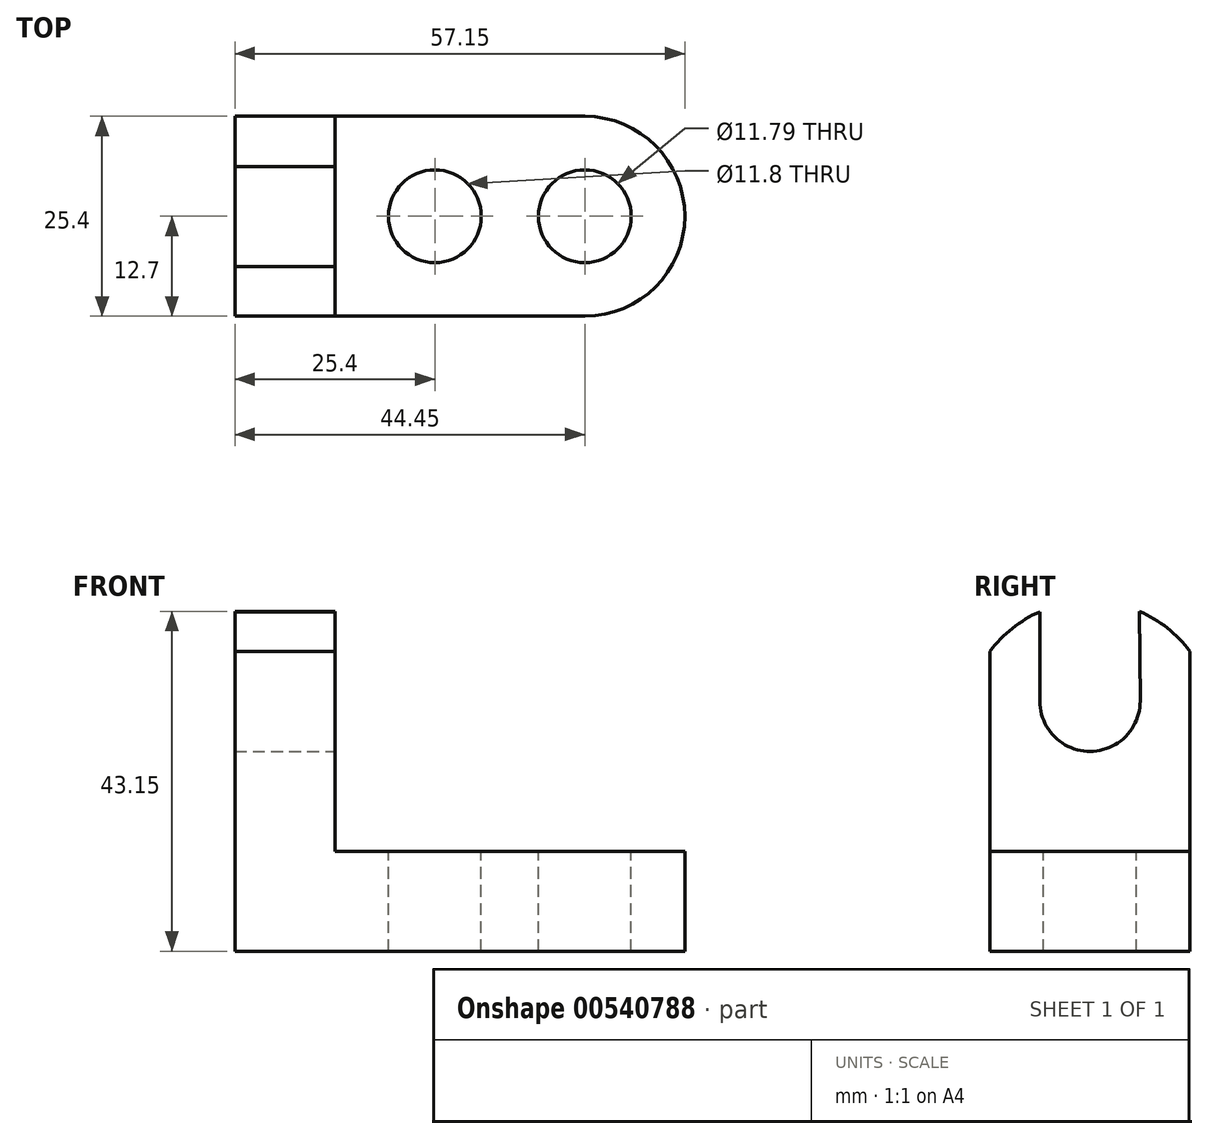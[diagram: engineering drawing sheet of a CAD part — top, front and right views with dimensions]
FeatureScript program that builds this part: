
annotation { "Feature Type Name" : "Feature", "Feature Type Description" : "" }
export const myFeature = defineFeature(function(context is Context, id is Id, definition is map)
    precondition{}
    {
        {
            var Q0;
            Q0=qCreatedBy(makeId("Front.planeOp"),FACE);
            var sketch = newSketch(context, id + "F0", { "sketchPlane" : qUnion([Q0])});
            skLineSegment(sketch, "E0", {"start": v(0, 0) * mm, "end": v(0, 44.45) * mm});
            skLineSegment(sketch, "E1", {"start": v(0, 44.45) * mm, "end": v(12.7, 44.45) * mm});
            skLineSegment(sketch, "E2", {"start": v(12.7, 44.45) * mm, "end": v(12.7, 12.7) * mm});
            skLineSegment(sketch, "E3", {"start": v(12.7, 12.7) * mm, "end": v(57.15, 12.7) * mm});
            skLineSegment(sketch, "E4", {"start": v(57.15, 12.7) * mm, "end": v(57.15, 0) * mm});
            skLineSegment(sketch, "E5", {"start": v(57.15, 0) * mm, "end": v(0, 0) * mm});
            skSolve(sketch);
        }
        {
            var Q0;
            Q0=makeQuery(id+"F0.imprint","IMPRINT",FACE,{"disambiguationData":[TD([[makeQuery(id+"F0.imprint","IMPRINT",EDGE,{"derivedFrom":sQuery(id+"F0.wireOp",EDGE,"E0")}),-1.0]])]});
            extrude(context, id + "F1", {"entities" : qUnion([Q0]), "depth" : 25.4 * mm, "offsetDistance" : 25.4 * mm});
        }
        {
            var Q0;
            Q0=makeQuery(id+"F1.opExtrude","SWEPT_FACE",FACE,{"disambiguationData":[OSD([sQuery(id+"F0.wireOp",EDGE,"E3")])]});
            var sketch = newSketch(context, id + "F2", { "sketchPlane" : qUnion([Q0])});
            skLineSegment(sketch, "E6", {"start": v(57.15, -12.7) * mm, "end": v(44.45, -12.7) * mm});
            skArc(sketch, "E7", {"start": v(44.45, -25.4) * mm, "mid": v(57.15, -12.7) * mm, "end": v(44.45, 0) * mm});
            skSolve(sketch);
        }
        {
            var Q0;
            {var subQ0=sQuery(id+"F2.wireOp",EDGE,"E7");var subQ1=sQuery(id+"F0.wireOp",EDGE,"E3");var subQ4=makeQuery(id+"F1.opExtrude","CAP_EDGE",EDGE,{"disambiguationData":[OSD([subQ1])],"isStart":true});var subQ5=makeQuery(id+"F2.imprint","INTERSECT",VERTEX,{"derivedFrom":[subQ4,subQ0]});Q0=makeQuery(id+"F2.imprint","IMPRINT",FACE,{"disambiguationData":[TD([[makeQuery(id+"F2.imprint","IMPRINT",EDGE,{"disambiguationData":[TD([[subQ5,1.0]])],"derivedFrom":subQ0}),-1.0]])]});}
            var Q1;
            {var subQ0=sQuery(id+"F2.wireOp",EDGE,"E7");var subQ1=sQuery(id+"F0.wireOp",EDGE,"E3");var subQ4=makeQuery(id+"F1.opExtrude","CAP_EDGE",EDGE,{"disambiguationData":[OSD([subQ1])],"isStart":false});var subQ5=makeQuery(id+"F2.imprint","INTERSECT",VERTEX,{"derivedFrom":[subQ4,subQ0]});Q1=makeQuery(id+"F2.imprint","IMPRINT",FACE,{"disambiguationData":[TD([[makeQuery(id+"F2.imprint","IMPRINT",EDGE,{"disambiguationData":[TD([[subQ5,-1.0]])],"derivedFrom":subQ0}),-1.0]])]});}
            extrude(context, id + "F3", {"entities" : qUnion([Q0, Q1]), "operationType" : NewBodyOperationType.REMOVE, "oppositeDirection" : true, "depth" : 25.4 * mm, "offsetDistance" : 25.4 * mm});
        }
        {
            var Q0;
            Q0=makeQuery(id+"F1.opExtrude","SWEPT_FACE",FACE,{"disambiguationData":[OSD([sQuery(id+"F0.wireOp",EDGE,"E2")])]});
            var sketch = newSketch(context, id + "F4", { "sketchPlane" : qUnion([Q0])});
            skLineSegment(sketch, "E8", {"start": v(-12.7, 44.45) * mm, "end": v(-12.7, 38.1) * mm});
            skArc(sketch, "E9", {"start": v(0, 38.1) * mm, "mid": v(-12.7, 44.45) * mm, "end": v(-25.4, 38.1) * mm});
            skSolve(sketch);
        }
        {
            var Q0;
            {var subQ0=sQuery(id+"F4.wireOp",EDGE,"E9");var subQ1=sQuery(id+"F0.wireOp",EDGE,"E2");var subQ4=makeQuery(id+"F1.opExtrude","CAP_EDGE",EDGE,{"disambiguationData":[OSD([subQ1])],"isStart":false});var subQ5=makeQuery(id+"F4.imprint","INTERSECT",VERTEX,{"derivedFrom":[subQ4,subQ0]});Q0=makeQuery(id+"F4.imprint","IMPRINT",FACE,{"disambiguationData":[TD([[makeQuery(id+"F4.imprint","IMPRINT",EDGE,{"disambiguationData":[TD([[subQ5,1.0]])],"derivedFrom":subQ0}),-1.0]])]});}
            var Q1;
            {var subQ0=sQuery(id+"F4.wireOp",EDGE,"E9");var subQ1=sQuery(id+"F0.wireOp",EDGE,"E2");var subQ4=makeQuery(id+"F1.opExtrude","CAP_EDGE",EDGE,{"disambiguationData":[OSD([subQ1])],"isStart":true});var subQ5=makeQuery(id+"F4.imprint","INTERSECT",VERTEX,{"derivedFrom":[subQ4,subQ0]});Q1=makeQuery(id+"F4.imprint","IMPRINT",FACE,{"disambiguationData":[TD([[makeQuery(id+"F4.imprint","IMPRINT",EDGE,{"disambiguationData":[TD([[subQ5,-1.0]])],"derivedFrom":subQ0}),-1.0]])]});}
            extrude(context, id + "F5", {"entities" : qUnion([Q0, Q1]), "operationType" : NewBodyOperationType.REMOVE, "oppositeDirection" : true, "depth" : 25.4 * mm, "offsetDistance" : 25.4 * mm});
        }
        {
            var Q0;
            Q0=makeQuery(id+"F1.opExtrude","SWEPT_FACE",FACE,{"disambiguationData":[OSD([sQuery(id+"F0.wireOp",EDGE,"E2")])]});
            var sketch = newSketch(context, id + "F6", { "sketchPlane" : qUnion([Q0])});
            skLineSegment(sketch, "E10", {"start": v(-12.7, 44.45) * mm, "end": v(-12.7, 31.75) * mm});
            skCircle(sketch, "E11", {"center": v(-12.7, 31.75) * mm, "radius": 6.37 * mm});
            skLineSegment(sketch, "E12", {"start": v(-12.7, 31.75) * mm, "end": v(-25.4, 31.75) * mm});
            skLineSegment(sketch, "E13", {"start": v(-19.07, 31.75) * mm, "end": v(-19.07, 43.12) * mm});
            skLineSegment(sketch, "E14", {"start": v(-6.33, 31.8) * mm, "end": v(0, 31.8) * mm});
            skLineSegment(sketch, "E15", {"start": v(-6.33, 31.8) * mm, "end": v(-6.4, 43.15) * mm});
            skLineSegment(sketch, "E16", {"start": v(-13.2, 25.4) * mm, "end": v(-13.2, 12.7) * mm});
            skLineSegment(sketch, "E17", {"start": v(-12.7, 31.75) * mm, "end": v(-13.2, 25.4) * mm});
            skSolve(sketch);
        }
        {
            var Q0;
            {var subQ8=sQuery(id+"F6.wireOp",EDGE,"E13");Q0=makeQuery(id+"F6.imprint","IMPRINT",FACE,{"disambiguationData":[TD([[makeQuery(id+"F6.imprint","IMPRINT",EDGE,{"derivedFrom":subQ8}),-1.0]])]});}
            var Q1;
            {var subQ8=sQuery(id+"F6.wireOp",EDGE,"E15");Q1=makeQuery(id+"F6.imprint","IMPRINT",FACE,{"disambiguationData":[TD([[makeQuery(id+"F6.imprint","IMPRINT",EDGE,{"derivedFrom":subQ8}),1.0]])]});}
            var Q2;
            {var subQ0=sQuery(id+"F6.wireOp",EDGE,"E12");var subQ1=sQuery(id+"F6.wireOp",EDGE,"E10");var subQ2=makeQuery(id+"F6.imprint","INTERSECT",VERTEX,{"derivedFrom":[subQ1,subQ0]});Q2=makeQuery(id+"F6.imprint","IMPRINT",FACE,{"disambiguationData":[TD([[makeQuery(id+"F6.imprint","IMPRINT",EDGE,{"disambiguationData":[TD([[subQ2,1.0]])],"derivedFrom":subQ1}),1.0]])]});}
            var Q3;
            {var subQ0=sQuery(id+"F6.wireOp",EDGE,"E12");var subQ1=sQuery(id+"F6.wireOp",EDGE,"E10");var subQ2=makeQuery(id+"F6.imprint","INTERSECT",VERTEX,{"derivedFrom":[subQ1,subQ0]});Q3=makeQuery(id+"F6.imprint","IMPRINT",FACE,{"disambiguationData":[TD([[makeQuery(id+"F6.imprint","IMPRINT",EDGE,{"disambiguationData":[TD([[subQ2,1.0]])],"derivedFrom":subQ1}),-1.0]])]});}
            var Q4;
            {var subQ3=sQuery(id+"F6.wireOp",EDGE,"E17");Q4=makeQuery(id+"F6.imprint","IMPRINT",FACE,{"disambiguationData":[TD([[makeQuery(id+"F6.imprint","IMPRINT",EDGE,{"derivedFrom":subQ3}),-1.0]])]});}
            extrude(context, id + "F7", {"entities" : qUnion([Q0, Q1, Q2, Q3, Q4]), "operationType" : NewBodyOperationType.REMOVE, "oppositeDirection" : true, "depth" : 25.4 * mm, "offsetDistance" : 25.4 * mm});
        }
        {
            var Q0;
            Q0=makeQuery(id+"F1.opExtrude","SWEPT_FACE",FACE,{"disambiguationData":[OSD([sQuery(id+"F0.wireOp",EDGE,"E3")])]});
            var sketch = newSketch(context, id + "F8", { "sketchPlane" : qUnion([Q0])});
            skCircle(sketch, "E18", {"center": v(25.4, -12.7) * mm, "radius": 5.9 * mm});
            skCircle(sketch, "E19", {"center": v(44.45, -12.7) * mm, "radius": 5.9 * mm});
            skLineSegment(sketch, "E20", {"start": v(25.4, -12.7) * mm, "end": v(25.4, -25.4) * mm});
            skLineSegment(sketch, "E21", {"start": v(44.45, -12.7) * mm, "end": v(44.45, -25.4) * mm});
            skLineSegment(sketch, "E22", {"start": v(25.4, -12.7) * mm, "end": v(57.15, -12.7) * mm});
            skLineSegment(sketch, "E23", {"start": v(44.45, -12.7) * mm, "end": v(57.15, -12.7) * mm});
            skSolve(sketch);
        }
        {
            var Q0;
            {var subQ0=sQuery(id+"F8.wireOp",EDGE,"E20");var subQ1=sQuery(id+"F8.wireOp",EDGE,"E18");var subQ2=makeQuery(id+"F8.imprint","INTERSECT",VERTEX,{"derivedFrom":[subQ1,subQ0]});Q0=makeQuery(id+"F8.imprint","IMPRINT",FACE,{"disambiguationData":[TD([[makeQuery(id+"F8.imprint","IMPRINT",EDGE,{"disambiguationData":[TD([[subQ2,1.0]])],"derivedFrom":subQ1}),1.0]])]});}
            var Q1;
            {var subQ0=sQuery(id+"F8.wireOp",EDGE,"E20");var subQ1=sQuery(id+"F8.wireOp",EDGE,"E18");var subQ2=makeQuery(id+"F8.imprint","INTERSECT",VERTEX,{"derivedFrom":[subQ1,subQ0]});Q1=makeQuery(id+"F8.imprint","IMPRINT",FACE,{"disambiguationData":[TD([[makeQuery(id+"F8.imprint","IMPRINT",EDGE,{"disambiguationData":[TD([[subQ2,-1.0]])],"derivedFrom":subQ1}),1.0]])]});}
            var Q2;
            {var subQ0=sQuery(id+"F8.wireOp",EDGE,"E23");var subQ1=sQuery(id+"F8.wireOp",EDGE,"E19");var subQ2=makeQuery(id+"F8.imprint","INTERSECT",VERTEX,{"derivedFrom":[subQ1,subQ0]});Q2=makeQuery(id+"F8.imprint","IMPRINT",FACE,{"disambiguationData":[TD([[makeQuery(id+"F8.imprint","IMPRINT",EDGE,{"disambiguationData":[TD([[subQ2,1.0]])],"derivedFrom":subQ1}),1.0]])]});}
            var Q3;
            {var subQ0=sQuery(id+"F8.wireOp",EDGE,"E22");var subQ1=sQuery(id+"F8.wireOp",EDGE,"E19");var subQ2=makeQuery(id+"F8.imprint","INTERSECT",VERTEX,{"derivedFrom":[subQ1,subQ0]});Q3=makeQuery(id+"F8.imprint","IMPRINT",FACE,{"disambiguationData":[TD([[makeQuery(id+"F8.imprint","IMPRINT",EDGE,{"disambiguationData":[TD([[subQ2,1.0]])],"derivedFrom":subQ1}),1.0]])]});}
            var Q4;
            {var subQ0=sQuery(id+"F8.wireOp",EDGE,"E22");var subQ1=sQuery(id+"F8.wireOp",EDGE,"E19");var subQ2=makeQuery(id+"F8.imprint","INTERSECT",VERTEX,{"derivedFrom":[subQ1,subQ0]});Q4=makeQuery(id+"F8.imprint","IMPRINT",FACE,{"disambiguationData":[TD([[makeQuery(id+"F8.imprint","IMPRINT",EDGE,{"disambiguationData":[TD([[subQ2,-1.0]])],"derivedFrom":subQ1}),1.0]])]});}
            extrude(context, id + "F9", {"entities" : qUnion([Q0, Q1, Q2, Q3, Q4]), "operationType" : NewBodyOperationType.REMOVE, "oppositeDirection" : true, "depth" : 25.4 * mm, "offsetDistance" : 25.4 * mm});
        }
    });
